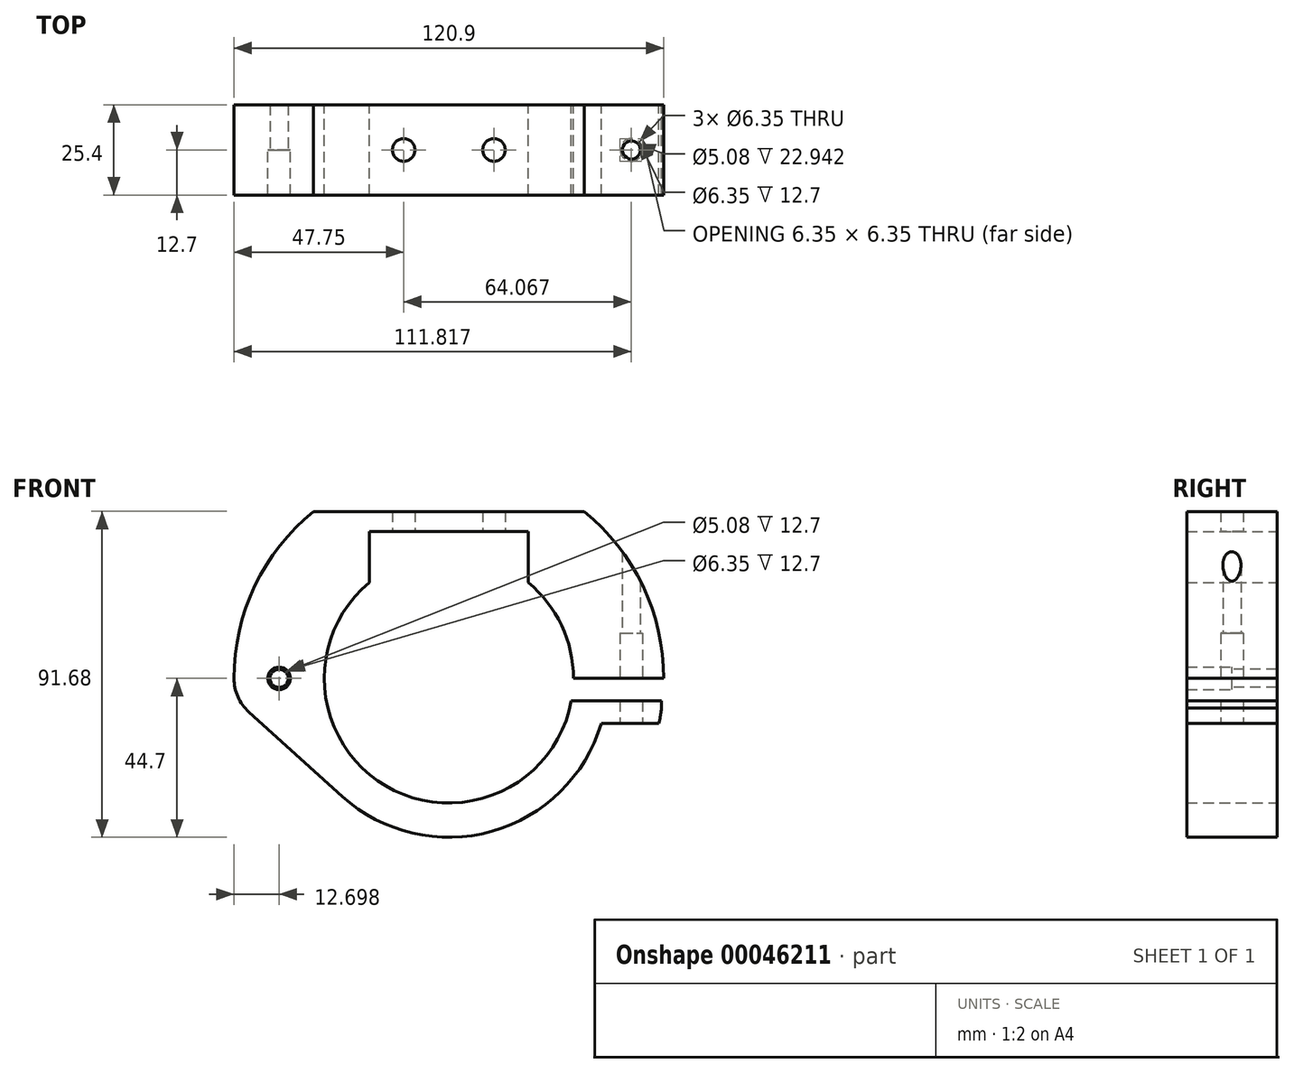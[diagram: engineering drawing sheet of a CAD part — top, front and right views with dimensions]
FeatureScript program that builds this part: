
annotation { "Feature Type Name" : "Feature", "Feature Type Description" : "" }
export const myFeature = defineFeature(function(context is Context, id is Id, definition is map)
    precondition{}
    {
        {
            var Q0;
            Q0=qCreatedBy(makeId("Front.planeOp"),FACE);
            var sketch = newSketch(context, id + "F0", { "sketchPlane" : qUnion([Q0])});
            skArc(sketch, "E0", {"start": v(35.05, 0) * mm, "mid": v(31.72, 14.92) * mm, "end": v(22.35, 27) * mm});
            skArc(sketch, "E1", {"start": v(-29.96, -33.18) * mm, "mid": v(12.1, -43.03) * mm, "end": v(42.86, -12.7) * mm});
            skPoint(sketch, "E2.orphan", {"position": v(0, 35.05) * mm});
            skPoint(sketch, "E3.end.orphan", {"position": v(60.45, 0) * mm});
            skPoint(sketch, "E4.top.start.orphan", {"position": v(59.87, -6.35) * mm});
            skPoint(sketch, "E5.right.end.orphan", {"position": v(59.87, -12.7) * mm});
            skCircle(sketch, "E6", {"center": v(-47.75, 0) * mm, "radius": 12.7 * mm});
            skLineSegment(sketch, "E7", {"start": v(34.47, -6.35) * mm, "end": v(59.87, -6.35) * mm});
            skLineSegment(sketch, "E8", {"start": v(42.86, -12.7) * mm, "end": v(59.87, -12.7) * mm});
            skLineSegment(sketch, "E9", {"start": v(59.87, -12.7) * mm, "end": v(59.87, -6.35) * mm});
            skLineSegment(sketch, "E10", {"start": v(35.05, 0) * mm, "end": v(60.45, 0) * mm});
            skPoint(sketch, "E11.top.end.orphan", {"position": v(60.45, 46.98) * mm});
            skLineSegment(sketch, "E12.top", {"start": v(-38.04, 46.98) * mm, "end": v(38.04, 46.98) * mm});
            skLineSegment(sketch, "E13", {"start": v(-56.26, -9.43) * mm, "end": v(-29.96, -33.18) * mm});
            skPoint(sketch, "E14.top.end.orphan", {"position": v(60.45, 9.53) * mm});
            skCircle(sketch, "E15", {"center": v(-47.75, 0) * mm, "radius": 2.54 * mm});
            skCircle(sketch, "E16", {"center": v(-47.75, 0) * mm, "radius": 3.18 * mm});
            skLineSegment(sketch, "E17.rect.bottom", {"start": v(-22.35, 41.32) * mm, "end": v(22.35, 41.32) * mm});
            skLineSegment(sketch, "E17.rect.left", {"start": v(-22.35, 41.32) * mm, "end": v(-22.35, 27) * mm});
            skLineSegment(sketch, "E17.rect.right", {"start": v(22.35, 41.32) * mm, "end": v(22.35, 27) * mm});
            skArc(sketch, "E18.trimOffspring", {"start": v(-22.35, 27) * mm, "mid": v(-17.74, -30.23) * mm, "end": v(34.47, -6.35) * mm});
            skPoint(sketch, "E19.trimOffspring.end.orphan", {"position": v(-22.35, -41.32) * mm});
            skPoint(sketch, "E20.trimOffspring.end.orphan", {"position": v(22.35, -41.32) * mm});
            skArc(sketch, "E21", {"start": v(-38.04, 46.98) * mm, "mid": v(0, -60.45) * mm, "end": v(38.04, 46.98) * mm});
            skSolve(sketch);
        }
        {
            var Q0;
            {var subQ4=sQuery(id+"F0.wireOp",EDGE,"E10");Q0=makeQuery(id+"F0.imprint","IMPRINT",FACE,{"disambiguationData":[TD([[makeQuery(id+"F0.imprint","IMPRINT",EDGE,{"derivedFrom":subQ4}),1.0]])]});}
            extrude(context, id + "F1", {"entities" : qUnion([Q0]), "depth" : 12.7 * mm});
        }
        {
            var Q0;
            Q0=makeQuery(id+"F1.opExtrude","CAP_FACE",FACE,{"disambiguationData":[OSD([sQuery(id+"F0.wireOp",EDGE,"E0"),sQuery(id+"F0.wireOp",EDGE,"E6"),sQuery(id+"F0.wireOp",EDGE,"E10"),sQuery(id+"F0.wireOp",EDGE,"E12.top"),sQuery(id+"F0.wireOp",EDGE,"E12.left"),sQuery(id+"F0.wireOp",EDGE,"E12.right")])],"isStart":false});
            var Q1;
            Q1=makeQuery(id+"F0.imprint","IMPRINT",FACE,{"disambiguationData":[TD([[makeQuery(id+"F0.imprint","IMPRINT",EDGE,{"derivedFrom":sQuery(id+"F0.wireOp",EDGE,"E16")}),-1.0]])]});
            var Q2;
            {var subQ4=sQuery(id+"F0.wireOp",EDGE,"E10");Q2=makeQuery(id+"F0.imprint","IMPRINT",FACE,{"disambiguationData":[TD([[makeQuery(id+"F0.imprint","IMPRINT",EDGE,{"derivedFrom":subQ4}),1.0]])]});}
            var Q3;
            Q3=makeQuery(id+"F0.imprint","IMPRINT",FACE,{"disambiguationData":[TD([[makeQuery(id+"F0.imprint","IMPRINT",EDGE,{"derivedFrom":sQuery(id+"F0.wireOp",EDGE,"E15")}),-1.0]])]});
            extrude(context, id + "F2", {"entities" : qUnion([Q0, Q1, Q2, Q3]), "operationType" : NewBodyOperationType.ADD, "oppositeDirection" : true, "depth" : 12.7 * mm});
        }
        {
            var Q0;
            Q0=makeQuery(id+"F0.imprint","IMPRINT",FACE,{"disambiguationData":[TD([[makeQuery(id+"F0.imprint","IMPRINT",EDGE,{"derivedFrom":sQuery(id+"F0.wireOp",EDGE,"E16")}),-1.0]])]});
            var Q1;
            Q1=makeQuery(id+"F0.imprint","IMPRINT",FACE,{"disambiguationData":[TD([[makeQuery(id+"F0.imprint","IMPRINT",EDGE,{"derivedFrom":sQuery(id+"F0.wireOp",EDGE,"E1")}),1.0]])]});
            extrude(context, id + "F3", {"entities" : qUnion([Q0, Q1]), "depth" : 12.7 * mm});
        }
        {
            var Q0;
            Q0=makeQuery(id+"F0.imprint","IMPRINT",FACE,{"disambiguationData":[TD([[makeQuery(id+"F0.imprint","IMPRINT",EDGE,{"derivedFrom":sQuery(id+"F0.wireOp",EDGE,"E1")}),1.0]])]});
            extrude(context, id + "F4", {"entities" : qUnion([Q0]), "operationType" : NewBodyOperationType.ADD, "oppositeDirection" : true, "depth" : 12.7 * mm});
        }
        {
            var Q0;
            {var subQ0=sQuery(id+"F0.wireOp",EDGE,"E8");Q0=makeQuery(id+"F4.boolean.opBoolean","MERGE",FACE,{"derivedFrom":[makeQuery(id+"F3.opExtrude","SWEPT_FACE",FACE,{"disambiguationData":[OSD([subQ0])]}),makeQuery(id+"F4.opExtrude","SWEPT_FACE",FACE,{"disambiguationData":[OSD([subQ0])]})]});}
            var sketch = newSketch(context, id + "F5", { "sketchPlane" : qUnion([Q0])});
            skLineSegment(sketch, "E22.bottom", {"start": v(42.86, -12.7) * mm, "end": v(42.86, -12.7) * mm});
            skLineSegment(sketch, "E22.top", {"start": v(42.86, 12.7) * mm, "end": v(42.86, 12.7) * mm});
            skLineSegment(sketch, "E22.left", {"start": v(42.86, -12.7) * mm, "end": v(42.86, 12.7) * mm});
            skLineSegment(sketch, "E22.right", {"start": v(42.86, -12.7) * mm, "end": v(42.86, 12.7) * mm});
            skCircle(sketch, "E23", {"center": v(51.37, 0) * mm, "radius": 3.18 * mm});
            skPoint(sketch, "E23.centerSnap0", {"position": v(42.86, 0) * mm});
            skPoint(sketch, "E23.centerSnap1", {"position": v(51.37, 12.7) * mm});
            skCircle(sketch, "E24", {"center": v(51.37, 0) * mm, "radius": 2.54 * mm});
            skSolve(sketch);
        }
        {
            var Q0;
            Q0=makeQuery(id+"F0.imprint","IMPRINT",FACE,{"disambiguationData":[TD([[makeQuery(id+"F0.imprint","IMPRINT",EDGE,{"derivedFrom":sQuery(id+"F0.wireOp",EDGE,"E16")}),-1.0]])]});
            var sketch = newSketch(context, id + "F6", { "sketchPlane" : qUnion([Q0])});
            skSolve(sketch);
        }
        {
            var Q0;
            Q0 = qSketchRegion(id + "F6", true);
            var Q1;
            Q1=makeQuery(id+"F5.imprint","IMPRINT",FACE,{"disambiguationData":[TD([[makeQuery(id+"F5.imprint","IMPRINT",EDGE,{"derivedFrom":sQuery(id+"F5.wireOp",EDGE,"E24")}),1.0]])]});
            extrude(context, id + "F7", {"entities" : qUnion([Q0, Q1]), "operationType" : NewBodyOperationType.REMOVE, "endBound" : BoundingType.THROUGH_ALL, "oppositeDirection" : true, "depth" : 6.35 * mm});
        }
        {
            var Q0;
            {var subQ0=sQuery(id+"F0.wireOp",EDGE,"E8");Q0=makeQuery(id+"F4.boolean.opBoolean","MERGE",FACE,{"derivedFrom":[makeQuery(id+"F3.opExtrude","SWEPT_FACE",FACE,{"disambiguationData":[OSD([subQ0])]}),makeQuery(id+"F4.opExtrude","SWEPT_FACE",FACE,{"disambiguationData":[OSD([subQ0])]})]});}
            var sketch = newSketch(context, id + "F8", { "sketchPlane" : qUnion([Q0])});
            skCircle(sketch, "E25", {"center": v(51.37, 0) * mm, "radius": 3.18 * mm});
            skSolve(sketch);
        }
        {
            var Q0;
            Q0=makeQuery(id+"F8.imprint","IMPRINT",FACE,{"disambiguationData":[TD([[makeQuery(id+"F8.imprint","IMPRINT",EDGE,{"derivedFrom":makeQuery(id+"F7.boolean.opBoolean","COPY",EDGE,{"derivedFrom":makeQuery(id+"F7.opExtrude","CAP_EDGE",EDGE,{"disambiguationData":[OSD([sQuery(id+"F5.wireOp",EDGE,"E24")])],"isStart":true})})}),1.0]])]});
            var Q1;
            Q1=makeQuery(id+"F8.imprint","IMPRINT",FACE,{"disambiguationData":[TD([[makeQuery(id+"F8.imprint","IMPRINT",EDGE,{"derivedFrom":sQuery(id+"F8.wireOp",EDGE,"E25")}),1.0]])]});
            extrude(context, id + "F9", {"entities" : qUnion([Q0, Q1]), "operationType" : NewBodyOperationType.REMOVE, "oppositeDirection" : true, "depth" : 25.4 * mm});
        }
        {
            var Q0;
            {var subQ0=sQuery(id+"F0.wireOp",EDGE,"E17.rect.bottom");Q0=makeQuery(id+"F2.boolean.opBoolean","MERGE",FACE,{"derivedFrom":[makeQuery(id+"F1.opExtrude","SWEPT_FACE",FACE,{"disambiguationData":[OSD([subQ0])]}),makeQuery(id+"F2.opExtrude","SWEPT_FACE",FACE,{"disambiguationData":[OSD([subQ0]),TDD([makeQuery(id+"F0.imprint","IMPRINT",EDGE,{"derivedFrom":subQ0})])]}),makeQuery(id+"F2.opExtrude","SWEPT_FACE",FACE,{"disambiguationData":[OSD([subQ0]),TDD([makeQuery(id+"F1.opExtrude","CAP_EDGE",EDGE,{"disambiguationData":[OSD([subQ0])],"isStart":false})])]})]});}
            var sketch = newSketch(context, id + "F10", { "sketchPlane" : qUnion([Q0])});
            skPoint(sketch, "E26.rect.middle", {"position": v(0, 0) * mm});
            skCircle(sketch, "E27", {"center": v(-12.7, 0) * mm, "radius": 3.18 * mm});
            skCircle(sketch, "E28", {"center": v(12.7, 0) * mm, "radius": 3.18 * mm});
            skPoint(sketch, "E29.orphan", {"position": v(-12.7, 3.17) * mm});
            skPoint(sketch, "E26.rect.bottom.end.orphan", {"position": v(-12.7, -3.18) * mm});
            skPoint(sketch, "E30.orphan", {"position": v(12.7, -3.17) * mm});
            skPoint(sketch, "E26.rect.left.end.orphan", {"position": v(12.7, 3.18) * mm});
            skSolve(sketch);
        }
        {
            var Q0;
            Q0=makeQuery(id+"F10.imprint","IMPRINT",FACE,{"disambiguationData":[TD([[makeQuery(id+"F10.imprint","IMPRINT",EDGE,{"derivedFrom":sQuery(id+"F10.wireOp",EDGE,"E28")}),1.0]])]});
            var Q1;
            Q1=makeQuery(id+"F10.imprint","IMPRINT",FACE,{"disambiguationData":[TD([[makeQuery(id+"F10.imprint","IMPRINT",EDGE,{"derivedFrom":sQuery(id+"F10.wireOp",EDGE,"E27")}),1.0]])]});
            extrude(context, id + "F11", {"entities" : qUnion([Q0, Q1]), "operationType" : NewBodyOperationType.REMOVE, "endBound" : BoundingType.UP_TO_NEXT, "oppositeDirection" : true, "depth" : 25.4 * mm});
        }
    });
